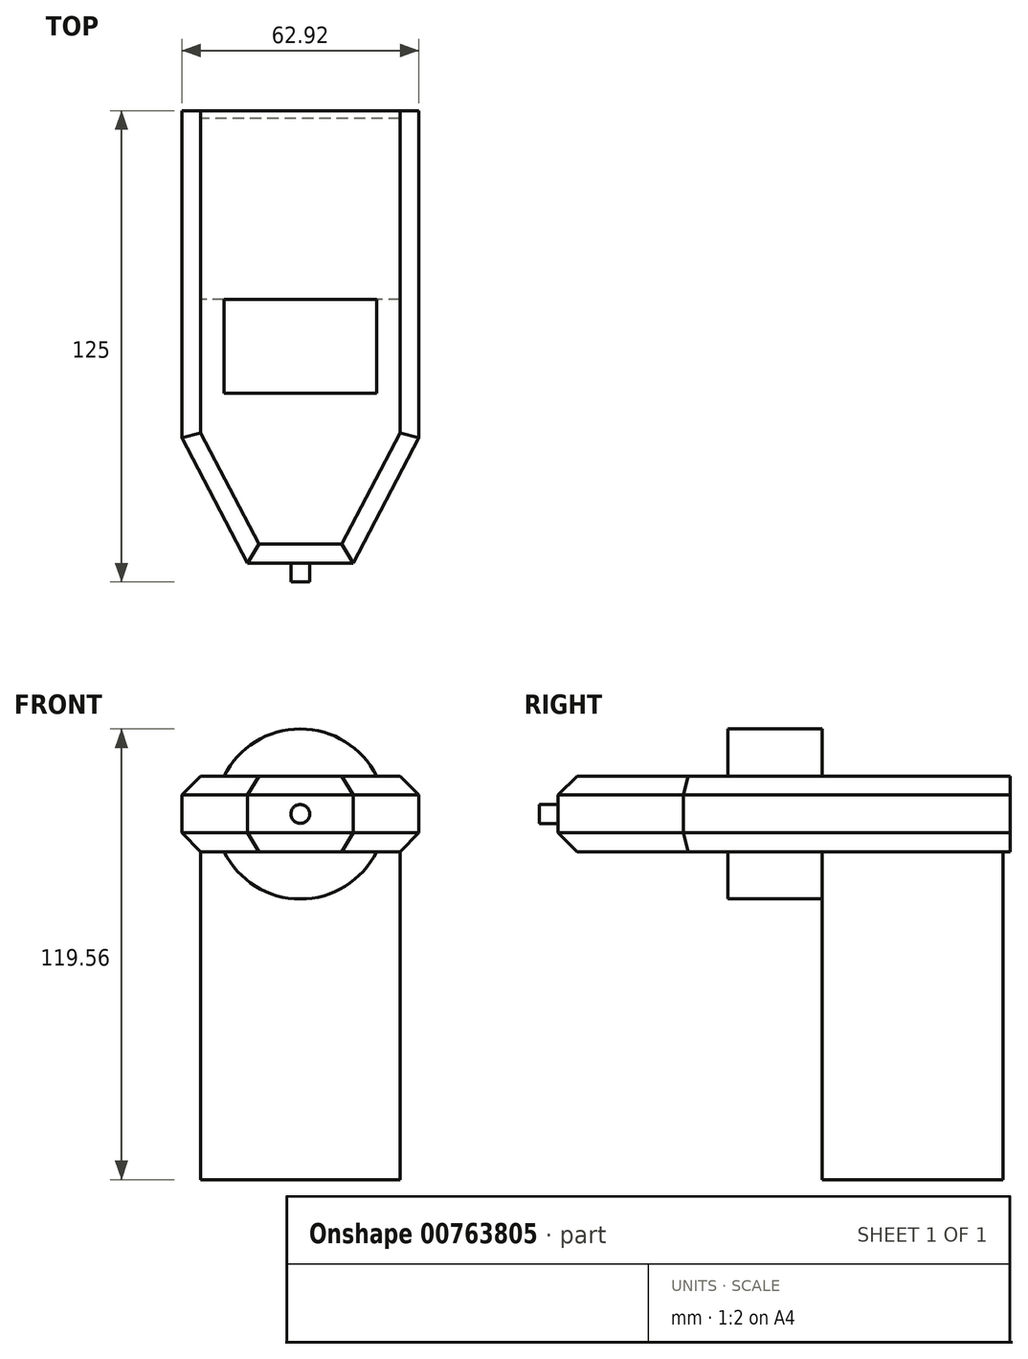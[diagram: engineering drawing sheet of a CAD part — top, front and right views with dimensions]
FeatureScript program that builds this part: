
annotation { "Feature Type Name" : "Feature", "Feature Type Description" : "" }
export const myFeature = defineFeature(function(context is Context, id is Id, definition is map)
    precondition{}
    {
        {
            var Q0;
            Q0=qCreatedBy(makeId("Front.planeOp"),FACE);
            var sketch = newSketch(context, id + "F0", { "sketchPlane" : qUnion([Q0])});
            skCircle(sketch, "E0", {"center": v(0, 0) * mm, "radius": 2.5 * mm});
            skSolve(sketch);
        }
        {
            var Q0;
            Q0=makeQuery(id+"F0.imprint","IMPRINT",FACE,{"disambiguationData":[TD([[makeQuery(id+"F0.imprint","IMPRINT",EDGE,{"derivedFrom":sQuery(id+"F0.wireOp",EDGE,"E0")}),1.0]])]});
            extrude(context, id + "F1", {"entities" : qUnion([Q0]), "depth" : 5 * mm, "offsetDistance" : 25 * mm});
        }
        {
            var Q0;
            Q0=qCreatedBy(makeId("Top.planeOp"),FACE);
            var sketch = newSketch(context, id + "F2", { "sketchPlane" : qUnion([Q0])});
            skLineSegment(sketch, "E1", {"start": v(0, 0) * mm, "end": v(-14.05, 0) * mm});
            skLineSegment(sketch, "E2", {"start": v(-14.05, 0) * mm, "end": v(-31.46, 33.22) * mm});
            skLineSegment(sketch, "E3", {"start": v(-31.46, 33.22) * mm, "end": v(-31.46, 120) * mm});
            skLineSegment(sketch, "E4", {"start": v(-31.46, 120) * mm, "end": v(0, 120) * mm});
            skLineSegment(sketch, "E5.MirrorCS", {"start": v(31.46, 120) * mm, "end": v(0, 120) * mm});
            skLineSegment(sketch, "E6.MirrorCS", {"start": v(31.46, 33.22) * mm, "end": v(31.46, 120) * mm});
            skLineSegment(sketch, "E7.MirrorCS", {"start": v(14.05, 0) * mm, "end": v(31.46, 33.22) * mm});
            skLineSegment(sketch, "E8.MirrorCS", {"start": v(0, 0) * mm, "end": v(14.05, 0) * mm});
            skSolve(sketch);
        }
        {
            var Q0;
            Q0 = qSketchRegion(id + "F2", true);
            extrude(context, id + "F3", {"entities" : qUnion([Q0]), "operationType" : NewBodyOperationType.ADD, "endBound" : BoundingType.SYMMETRIC, "depth" : 20 * mm, "offsetDistance" : 25 * mm});
        }
        {
            var Q0;
            Q0=makeQuery(id+"F3.opExtrude","CAP_EDGE",EDGE,{"disambiguationData":[OSD([sQuery(id+"F2.wireOp",EDGE,"E3")])],"isStart":true});
            var Q1;
            Q1=makeQuery(id+"F3.opExtrude","CAP_EDGE",EDGE,{"disambiguationData":[OSD([sQuery(id+"F2.wireOp",EDGE,"E2")])],"isStart":true});
            var Q2;
            Q2=makeQuery(id+"F3.opExtrude","CAP_EDGE",EDGE,{"disambiguationData":[OSD([sQuery(id+"F2.wireOp",EDGE,"E1"),sQuery(id+"F2.wireOp",EDGE,"E8.MirrorCS")])],"isStart":true});
            var Q3;
            Q3=makeQuery(id+"F3.opExtrude","CAP_EDGE",EDGE,{"disambiguationData":[OSD([sQuery(id+"F2.wireOp",EDGE,"E7.MirrorCS")])],"isStart":true});
            var Q4;
            Q4=makeQuery(id+"F3.opExtrude","CAP_EDGE",EDGE,{"disambiguationData":[OSD([sQuery(id+"F2.wireOp",EDGE,"E6.MirrorCS")])],"isStart":true});
            var Q5;
            Q5=makeQuery(id+"F3.opExtrude","CAP_EDGE",EDGE,{"disambiguationData":[OSD([sQuery(id+"F2.wireOp",EDGE,"E6.MirrorCS")])],"isStart":false});
            var Q6;
            Q6=makeQuery(id+"F3.opExtrude","CAP_EDGE",EDGE,{"disambiguationData":[OSD([sQuery(id+"F2.wireOp",EDGE,"E7.MirrorCS")])],"isStart":false});
            var Q7;
            Q7=makeQuery(id+"F3.opExtrude","CAP_EDGE",EDGE,{"disambiguationData":[OSD([sQuery(id+"F2.wireOp",EDGE,"E1"),sQuery(id+"F2.wireOp",EDGE,"E8.MirrorCS")])],"isStart":false});
            var Q8;
            Q8=makeQuery(id+"F3.opExtrude","CAP_EDGE",EDGE,{"disambiguationData":[OSD([sQuery(id+"F2.wireOp",EDGE,"E2")])],"isStart":false});
            var Q9;
            Q9=makeQuery(id+"F3.opExtrude","CAP_EDGE",EDGE,{"disambiguationData":[OSD([sQuery(id+"F2.wireOp",EDGE,"E3")])],"isStart":false});
            chamfer(context, id + "F4", {"entities" : qUnion([Q0, Q1, Q2, Q3, Q4, Q5, Q6, Q7, Q8, Q9]), "width" : 5 * mm, "tangentPropagation" : true});
        }
        {
            var Q0;
            Q0=qCreatedBy(makeId("Front.planeOp"),FACE);
            cPlane(context, id + "F5", {"entities" : qUnion([Q0]), "cplaneType" : CPlaneType.OFFSET, "offset" : 70 * mm, "oppositeDirection" : true, "width" : 150 * mm, "height" : 150 * mm});
        }
        {
            var Q0;
            Q0=qCreatedBy(id+"F5.planeOp",FACE);
            var sketch = newSketch(context, id + "F6", { "sketchPlane" : qUnion([Q0])});
            skCircle(sketch, "E9", {"center": v(0, 0) * mm, "radius": 22.56 * mm});
            skSolve(sketch);
        }
        {
            var Q0;
            Q0=makeQuery(id+"F6.imprint","IMPRINT",FACE,{"disambiguationData":[TD([[makeQuery(id+"F6.imprint","IMPRINT",EDGE,{"derivedFrom":sQuery(id+"F6.wireOp",EDGE,"E9")}),1.0]])]});
            extrude(context, id + "F7", {"entities" : qUnion([Q0]), "operationType" : NewBodyOperationType.ADD, "depth" : 25 * mm, "offsetDistance" : 25 * mm});
        }
        {
            var Q0;
            Q0=qCreatedBy(id+"F5.planeOp",FACE);
            var sketch = newSketch(context, id + "F8", { "sketchPlane" : qUnion([Q0])});
            skLineSegment(sketch, "E10", {"start": v(0, -10) * mm, "end": v(0, -97) * mm, "construction": true});
            skLineSegment(sketch, "E11", {"start": v(26.46, -10) * mm, "end": v(26.46, -97) * mm});
            skLineSegment(sketch, "E12", {"start": v(26.46, -97) * mm, "end": v(0, -97) * mm});
            skLineSegment(sketch, "E13", {"start": v(26.46, -10) * mm, "end": v(0, -10) * mm});
            skLineSegment(sketch, "E14.MirrorCS", {"start": v(-26.46, -10) * mm, "end": v(0, -10) * mm});
            skLineSegment(sketch, "E15.MirrorCS", {"start": v(-26.46, -10) * mm, "end": v(-26.46, -97) * mm});
            skLineSegment(sketch, "E16.MirrorCS", {"start": v(-26.46, -97) * mm, "end": v(0, -97) * mm});
            skSolve(sketch);
        }
        {
            var Q0;
            Q0=makeQuery(id+"F8.imprint","IMPRINT",FACE,{"disambiguationData":[TD([[makeQuery(id+"F8.imprint","IMPRINT",EDGE,{"derivedFrom":sQuery(id+"F8.wireOp",EDGE,"E11")}),-1.0]])]});
            extrude(context, id + "F9", {"entities" : qUnion([Q0]), "operationType" : NewBodyOperationType.ADD, "oppositeDirection" : true, "depth" : 48 * mm, "offsetDistance" : 25 * mm});
        }
    });
